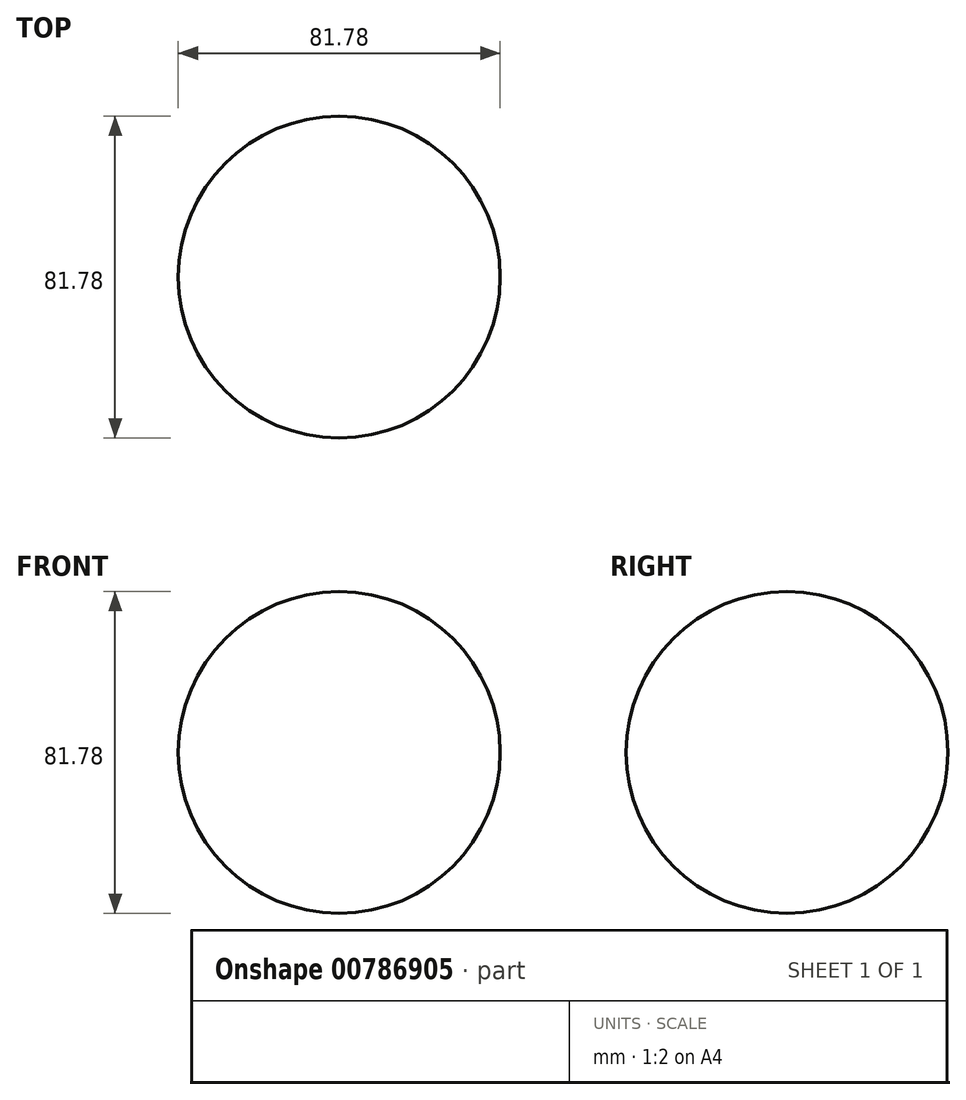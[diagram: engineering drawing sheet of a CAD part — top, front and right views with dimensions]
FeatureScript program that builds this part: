
annotation { "Feature Type Name" : "Feature", "Feature Type Description" : "" }
export const myFeature = defineFeature(function(context is Context, id is Id, definition is map)
    precondition{}
    {
        {
            var Q0;
            Q0=qCreatedBy(makeId("Front.planeOp"),FACE);
            var sketch = newSketch(context, id + "F0", { "sketchPlane" : qUnion([Q0])});
            skCircle(sketch, "E0", {"center": v(0, 0) * mm, "radius": 40.89 * mm});
            skLineSegment(sketch, "E1", {"start": v(0, 60.92) * mm, "end": v(0, -57.57) * mm});
            skSolve(sketch);
        }
        {
            var Q0;
            {var subQ0=sQuery(id+"F0.wireOp",EDGE,"E1");var subQ1=sQuery(id+"F0.wireOp",EDGE,"E0");var subQ2=makeQuery(id+"F0.imprint","INTERSECT",VERTEX,{"disambiguationData":[OD(0.0)],"derivedFrom":[subQ1,subQ0]});Q0=makeQuery(id+"F0.imprint","IMPRINT",FACE,{"disambiguationData":[TD([[makeQuery(id+"F0.imprint","IMPRINT",EDGE,{"disambiguationData":[TD([[subQ2,-1.0]])],"derivedFrom":subQ1}),1.0]])]});}
            var Q1;
            Q1=sQuery(id+"F0.wireOp",EDGE,"E1");
            revolve(context, id + "F1", {"surfaceOperationType" : NewSurfaceOperationType.NEW, "entities" : qUnion([Q0]), "axis" : qUnion([Q1]), "revolveType" : RevolveType.FULL});
        }
    });
